# Revit family: RA-NCX_Straight_DN15_RFA_1
name_source: partatom
category: Pipe Accessories
units: mm (PartAtom-declared; Revit-internal decimal feet)

## family parameters
Always vertical = Yes
Cut with Voids When Loaded = No
OmniClass Number = 23.65.55.14.17
OmniClass Title = Adjusting/Controlling Valves for Liquid Services
Part Type = Valve - Breaks Into
Round Connector Dimension = Use Diameter
Shared = No
Work Plane-Based = No

## types (2) — shared parameters
Connection = Internal Thread
D = 15 mm  [stored 0.0492126 ft]
DB1 = 26 mm
D_Thread = 23 mm  [stored 0.0754593 ft]
Description = Thermostatic Radiator Valve
H = 63 mm
H2 = 7 mm  [stored 0.0229659 ft]
Ha = 45 mm
IfcExportAs = IfcValveType
IfcExportType = RA-NCX
Kvs = 0.9 m³/h
L6 = 5 mm  [stored 0.0164042 ft]
LOD 200 = No
LOD 350 = Yes
L_1 = 10 mm  [stored 0.0328084 ft]
L_2 = 10 mm  [stored 0.0328084 ft]
L_Thread1 = 13 mm  [stored 0.0426509 ft]
L_Thread2 = 15 mm  [stored 0.0492126 ft]
Manufacturer = Danfoss
Max Differential Pressure = 0.6 bar
Max Medium Temperature = 120 ˚C
Max Operating Pressure = 10 bar
RV2 = 13 mm  [stored 0.0426509 ft]
RV4 = 15 mm  [stored 0.0492126 ft]
R_200 = 15 mm  [stored 0.0492126 ft]
R_200_1 = 17 mm
Setting Range = 1-7,N
URL = https://store.danfoss.com
Valve Body Material = Danfoss Brass (Chrome plated)
W = 35 mm

## per-type parameters (varying)
| type | DV1 | H1 | L | L1 | L2 | L3 | L4 | L5 | Model | Model Type | RV3 | RV5 | TL | Weight |
| RA-NCX_Straight_DN15_F_013G4248 | 21 mm  [stored 0.0688976 ft] | 15 mm  [stored 0.0492126 ft] | 82 mm  [stored 0.269029 ft] | 29 mm  [stored 0.0951444 ft] | 33 mm | 4 mm  [stored 0.0131234 ft] | 10 mm  [stored 0.0328084 ft] | 16 mm  [stored 0.0524934 ft] | 013G4248 | RA-NCX_Straight_DN15_F | 12 mm  [stored 0.0393701 ft] | 10 mm  [stored 0.0328084 ft] | 62 mm | 0.26 kg |
| RA-NCX_Straight_DN15_D_013G4238 | 22 mm  [stored 0.0721785 ft] | 14 mm  [stored 0.0459318 ft] | 95 mm | 37 mm  [stored 0.121391 ft] | 38 mm  [stored 0.124672 ft] | 2 mm  [stored 0.00656168 ft] | 19 mm  [stored 0.062336 ft] | 19 mm  [stored 0.062336 ft] | 013G4238 | RA-NCX_Straight_DN15_D | 13 mm  [stored 0.0426509 ft] | 11 mm  [stored 0.0360892 ft] | 75 mm | 0.28 kg |

note: [stored X ft] marks values corroborated as IEEE doubles in the binary element streams (Revit-internal decimal feet)

## geometry (parser evidence)
native form markers: Sweep x2
no freeform markers — native parametric forms only
